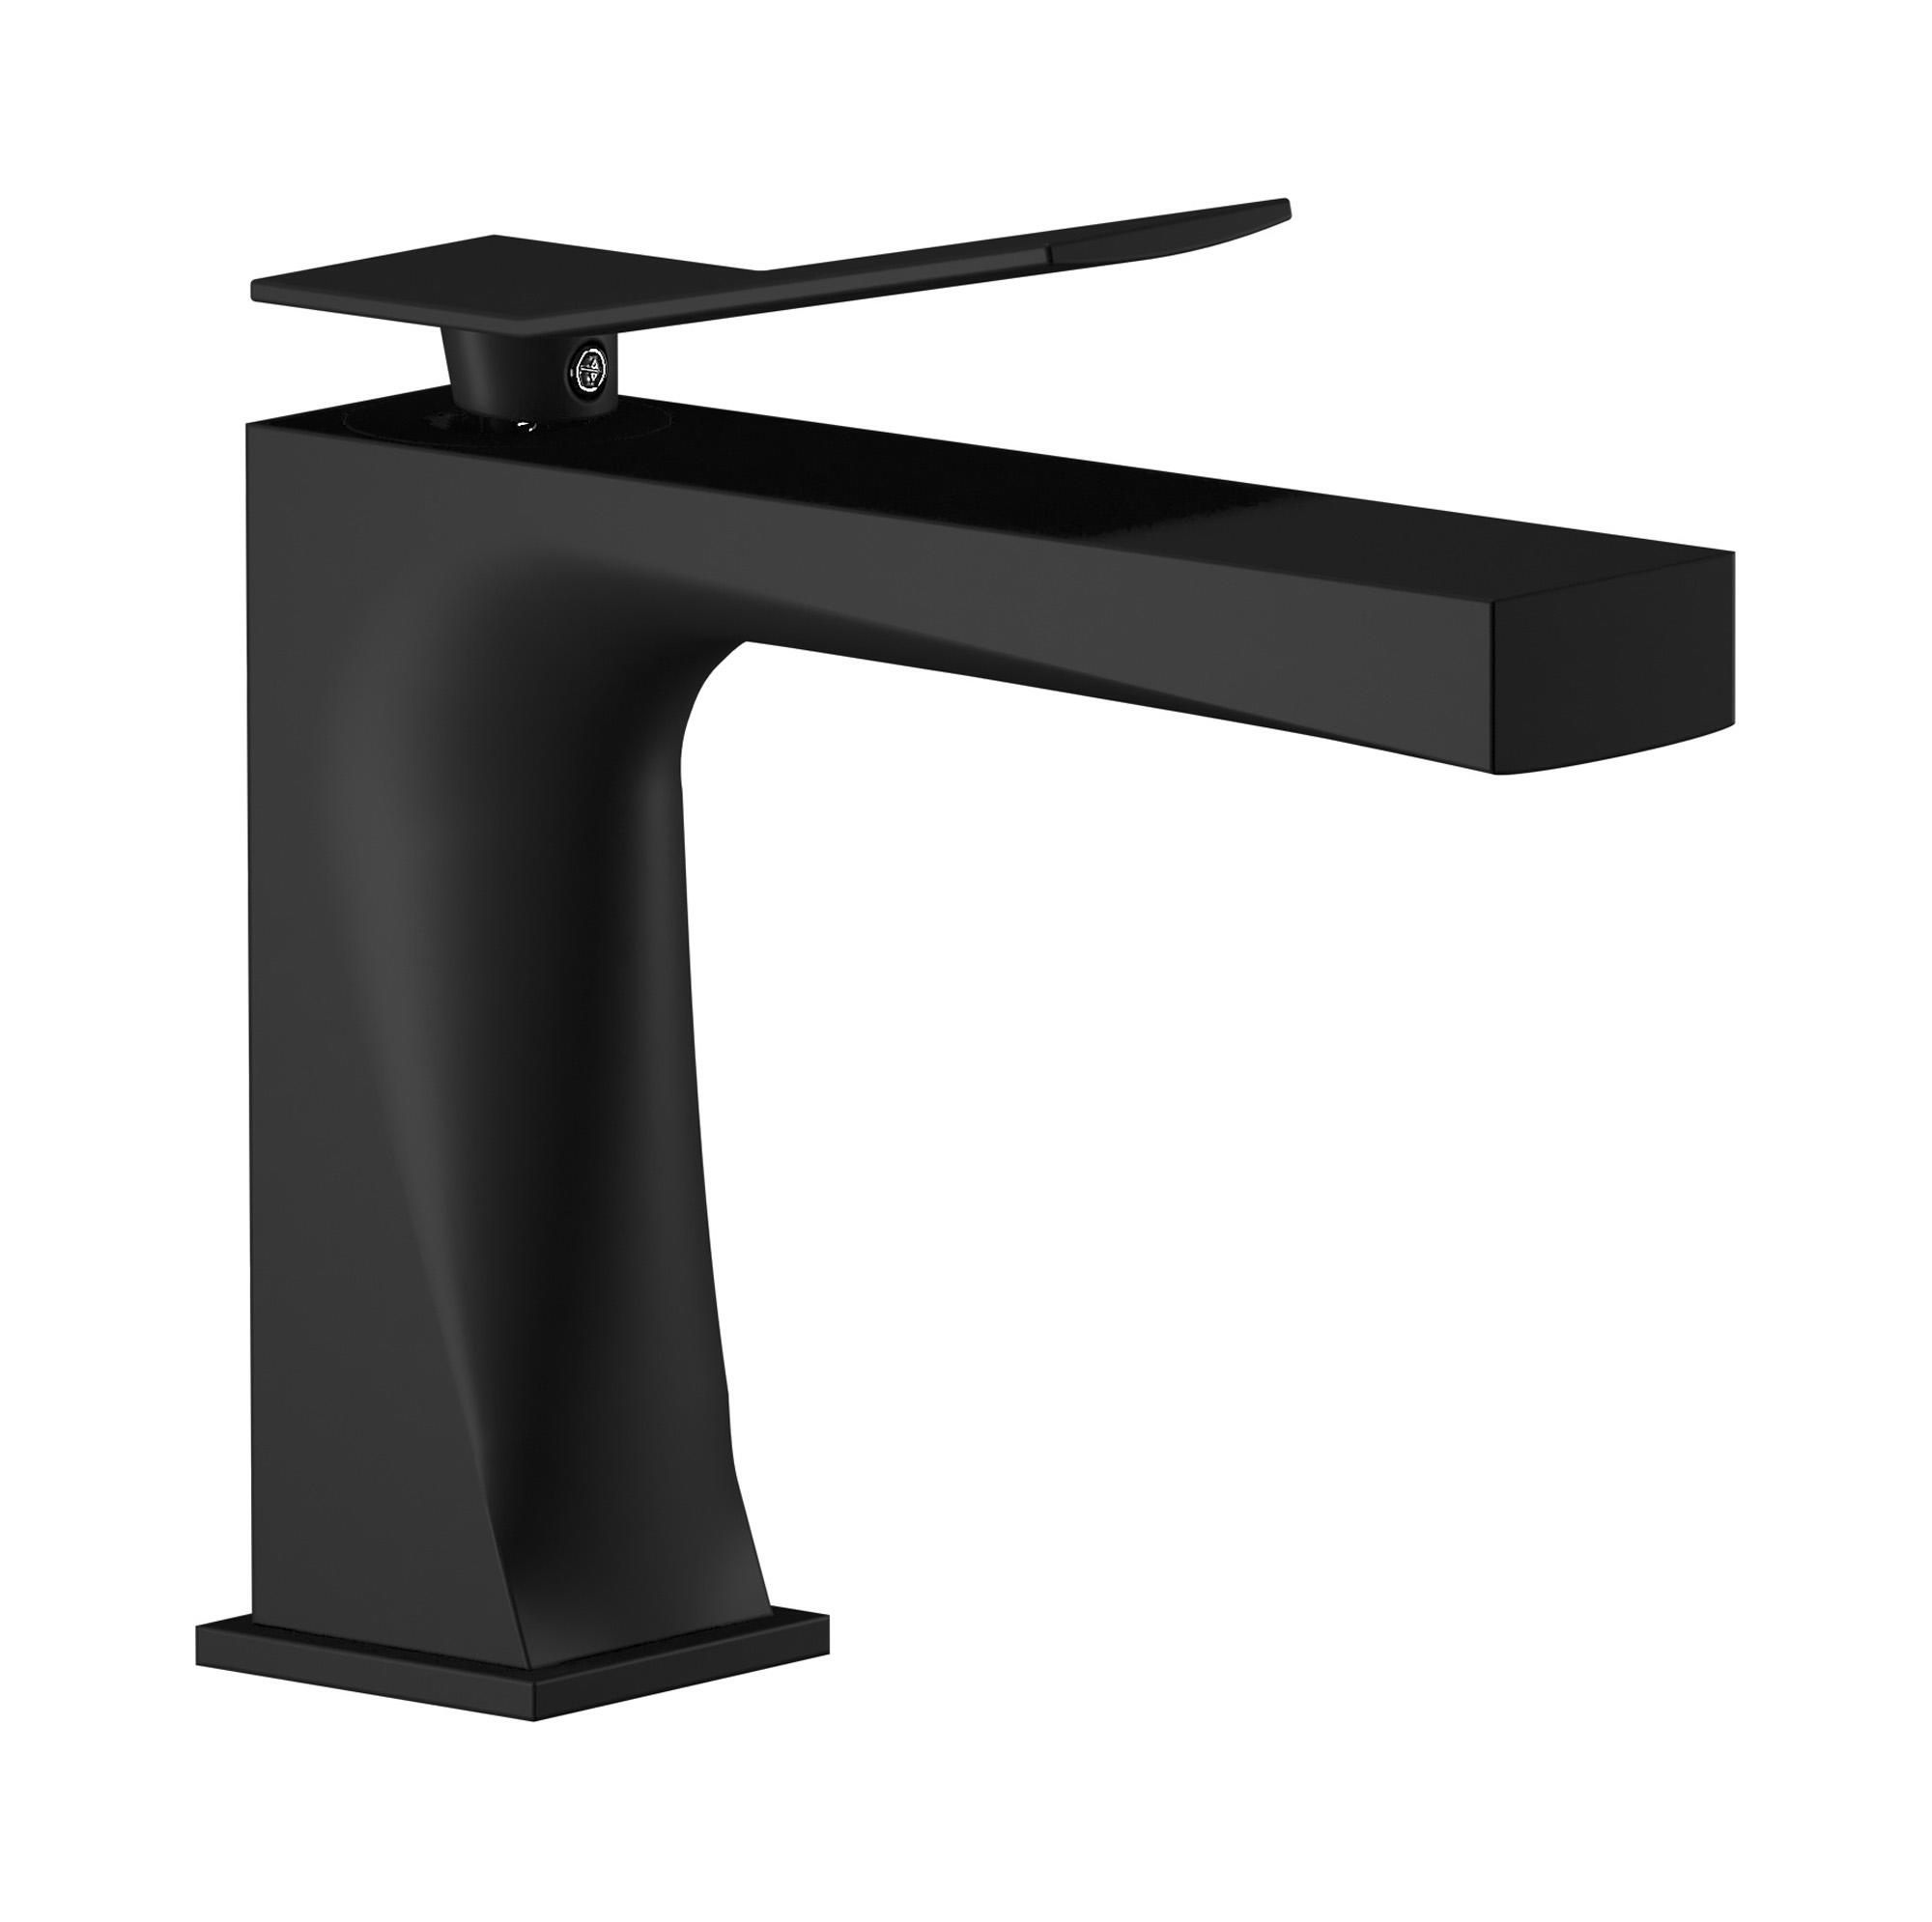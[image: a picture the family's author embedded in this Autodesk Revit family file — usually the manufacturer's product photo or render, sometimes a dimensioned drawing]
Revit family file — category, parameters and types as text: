
# Revit family: WA200
name_source: partatom
category: Apparecchi idraulici
units: mm (PartAtom-declared; Revit-internal decimal feet)

## family parameters
Basato su piano di lavoro = No
Condiviso = No
Mantieni orientamento annotazione = No
Numero OmniClass = 23.45.55.17
Punto di calcolo locali = No
Quota connettore circolare = Usa diametro
Sempre verticale = Sì
Taglio con vuoti quando caricato = No
Tipo di parte = Normale
Titolo OmniClass = Mixing Faucets

## types (12) — shared parameters
Cold water inlet = 10 mm  [stored 0.0328084 ft]
Commenti sul tipo = Washbasin mixer
Connessione CW = No
Connessione HW = No
Connessione di scarico = No
Connessione di ventilazione = No
Descrizione = Monohole washbasin mixer complete with drain
Hot water inlet = 10 mm  [stored 0.0328084 ft]
Produttore = IB Rubinetterie S.p.A.
URL = https://www.weareib.it
zero-valued in all types: Prospetto di default

## per-type parameters (varying)
| type | Finishes surface | Immagine tipo | Modello |
| Chrome | IB_Chrome | WA200CC.jpg | WA200CC |
| Matt white | IB_matt white | WA200BO.jpg | WA200BO |
| Matt black | IB_matt black | WA200NP.jpg | WA200NP |
| Brushed nickel | IB_Brushed nickel | WA200SS.jpg | WA200SS |
| Black chrome | IB_Black chrome | WA200CF.jpg | WA200CF |
| Brushed black chrome | IB_Brushed black chrome | WA200CS.jpg | WA200CS |
| Pale gold | IB_Pale gold | WA200II.jpg | WA200II |
| Brushed pale gold | IB_brushed pale gold | WA200IS.jpg | WA200IS |
| Rose gold | IB_Rose gold | WA200RS.jpg | WA200RS |
| Brushed rose gold | IB_Brushed rose gold | WA200SR.jpg | WA200SR |
| Gold | IB_gold | WA200OO.jpg | WA200OO |
| Brushed gold | IB_brushed gold | WA200OS.jpg | WA200OS |

note: [stored X ft] marks values corroborated as IEEE doubles in the binary element streams (Revit-internal decimal feet)
